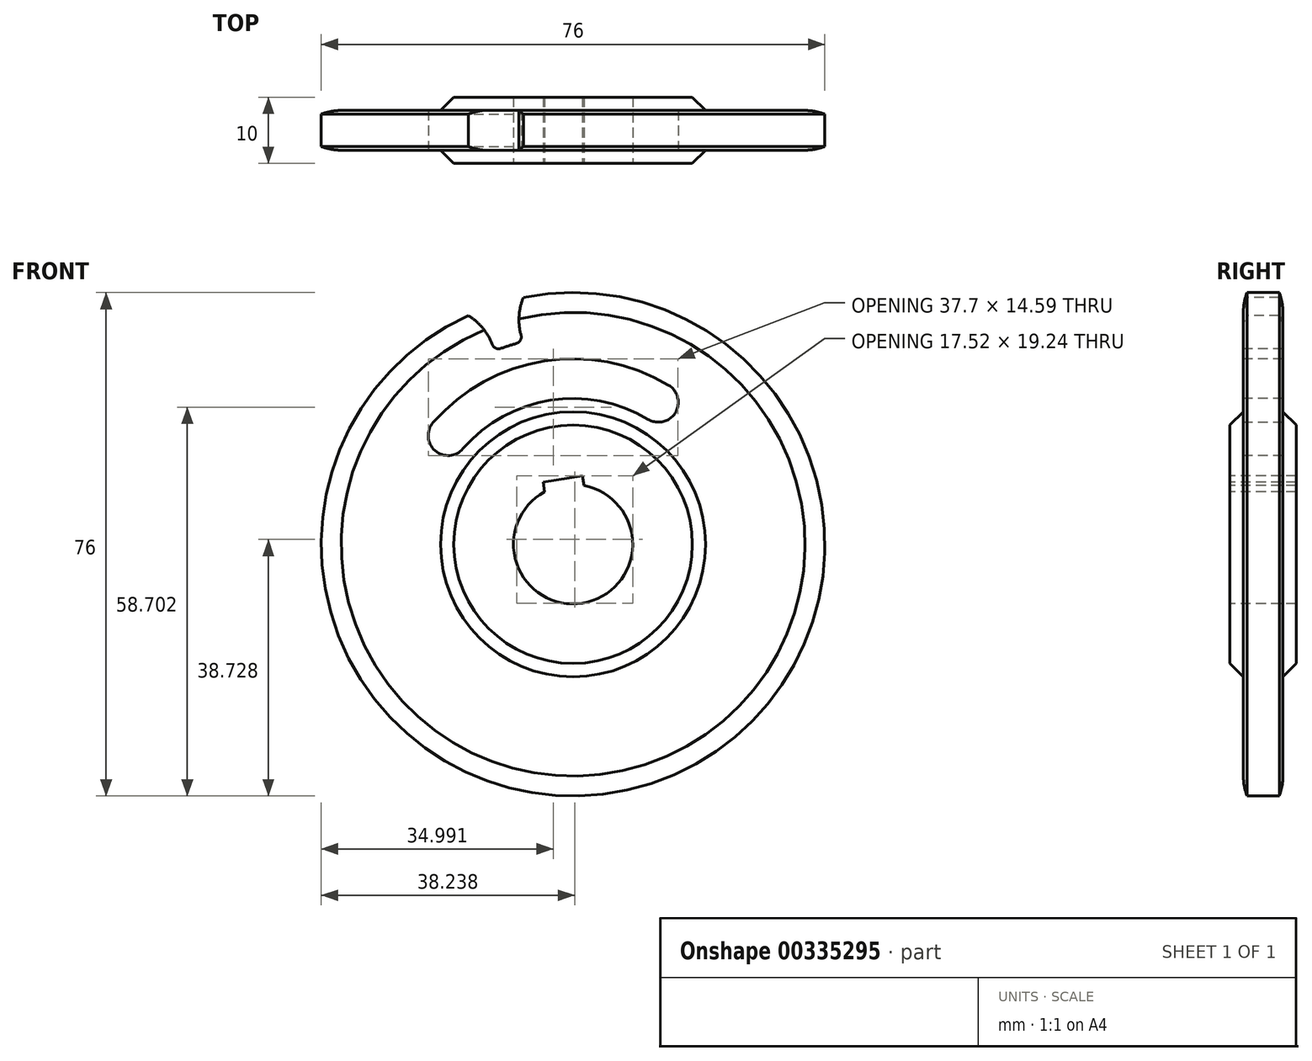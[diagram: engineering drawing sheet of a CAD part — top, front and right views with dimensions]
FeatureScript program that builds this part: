
annotation { "Feature Type Name" : "Feature", "Feature Type Description" : "" }
export const myFeature = defineFeature(function(context is Context, id is Id, definition is map)
    precondition{}
    {
        {
            var Q0;
            Q0=qCreatedBy(makeId("Front.planeOp"),FACE);
            var sketch = newSketch(context, id + "F0", { "sketchPlane" : qUnion([Q0])});
            skCircle(sketch, "E0", {"center": v(0, 0) * mm, "radius": 38 * mm});
            skSolve(sketch);
        }
        {
            var Q0;
            Q0=makeQuery(id+"F0.imprint","IMPRINT",FACE,{"disambiguationData":[TD([[makeQuery(id+"F0.imprint","IMPRINT",EDGE,{"derivedFrom":sQuery(id+"F0.wireOp",EDGE,"E0")}),1.0]])]});
            extrude(context, id + "F1", {"entities" : qUnion([Q0]), "depth" : 6 * mm, "symmetric" : true});
        }
        {
            var Q0;
            Q0=makeQuery(id+"F1.opExtrude","CAP_FACE",FACE,{"disambiguationData":[OSD([sQuery(id+"F0.wireOp",EDGE,"E0")])],"isStart":false});
            var sketch = newSketch(context, id + "F2", { "sketchPlane" : qUnion([Q0])});
            skLineSegment(sketch, "E1", {"start": v(0, 0) * mm, "end": v(0, 38) * mm, "construction": true});
            skArc(sketch, "E2", {"start": v(-1.57, 37.97) * mm, "mid": v(-0.79, 38) * mm, "end": v(0, 38) * mm, "construction": true});
            skCircle(sketch, "E3", {"center": v(0, 0) * mm, "radius": 35 * mm, "construction": true});
            skCircle(sketch, "E4", {"center": v(0, 0) * mm, "radius": 31.5 * mm, "construction": true});
            skArc(sketch, "E5", {"start": v(-1.58, 37.97) * mm, "mid": v(-2.67, 35.28) * mm, "end": v(-2.82, 32.39) * mm});
            skPoint(sketch, "E6", {"position": v(-2.75, 34.9) * mm});
            skLineSegment(sketch, "E7", {"start": v(0, 0) * mm, "end": v(-5.94, 37.53) * mm, "construction": true});
            skArc(sketch, "E8", {"start": v(-3.7, 31.28) * mm, "mid": v(-4.31, 31.2) * mm, "end": v(-4.93, 31.11) * mm});
            skPoint(sketch, "E9.visualSharp", {"position": v(-2.65, 31.39) * mm});
            skArc(sketch, "E9.filletArc", {"start": v(-3.7, 31.28) * mm, "mid": v(-3.03, 31.65) * mm, "end": v(-2.82, 32.39) * mm});
            skArc(sketch, "E10", {"start": v(-1.57, 37.97) * mm, "mid": v(-3.77, 37.81) * mm, "end": v(-5.94, 37.53) * mm});
            skArc(sketch, "E11.MirrorCS", {"start": v(-10.23, 36.6) * mm, "mid": v(-8.1, 37.13) * mm, "end": v(-5.94, 37.53) * mm});
            skArc(sketch, "E12.MirrorCS", {"start": v(-10.23, 36.6) * mm, "mid": v(-8.37, 34.38) * mm, "end": v(-7.32, 31.67) * mm});
            skArc(sketch, "E13.MirrorCS", {"start": v(-6.15, 30.9) * mm, "mid": v(-6.9, 31.04) * mm, "end": v(-7.32, 31.67) * mm});
            skArc(sketch, "E14.MirrorCS", {"start": v(-6.15, 30.9) * mm, "mid": v(-5.54, 31) * mm, "end": v(-4.93, 31.11) * mm});
            skSolve(sketch);
        }
        {
            var Q0;
            Q0=qSketchRegion(id+"F2",true);
            extrude(context, id + "F3", {"entities" : qUnion([Q0]), "operationType" : NewBodyOperationType.REMOVE, "oppositeDirection" : true, "depth" : 25 * mm});
        }
        {
            var Q0;
            Q0=qCreatedBy(makeId("Front.planeOp"),FACE);
            var sketch = newSketch(context, id + "F4", { "sketchPlane" : qUnion([Q0])});
            skCircle(sketch, "E15", {"center": v(0, 0) * mm, "radius": 18 * mm});
            skSolve(sketch);
        }
        {
            var Q0;
            Q0=qSketchRegion(id+"F4",true);
            extrude(context, id + "F5", {"entities" : qUnion([Q0]), "depth" : 10 * mm, "symmetric" : true});
        }
        {
            var Q0;
            Q0=makeQuery(id+"F1.opExtrude","SWEPT_BODY",BODY,{"disambiguationData":[OSD([sQuery(id+"F0.wireOp",EDGE,"E0")])]});
            var Q1;
            Q1=makeQuery(id+"F5.opExtrude","SWEPT_BODY",BODY,{"disambiguationData":[OSD([sQuery(id+"F4.wireOp",EDGE,"E15")])]});
            booleanBodies(context, id + "F6", {"operationType" : BooleanOperationType.UNION, "tools" : qUnion([Q0, Q1])});
        }
        {
            var Q0;
            Q0=makeQuery(id+"F6.opBoolean","INTERSECT",EDGE,{"derivedFrom":[makeQuery(id+"F1.opExtrude","CAP_FACE",FACE,{"disambiguationData":[OSD([sQuery(id+"F0.wireOp",EDGE,"E0")])],"isStart":true}),makeQuery(id+"F5.opExtrude","SWEPT_FACE",FACE,{"disambiguationData":[OSD([sQuery(id+"F4.wireOp",EDGE,"E15")])]})]});
            var Q1;
            Q1=makeQuery(id+"F6.opBoolean","INTERSECT",EDGE,{"derivedFrom":[makeQuery(id+"F1.opExtrude","CAP_FACE",FACE,{"disambiguationData":[OSD([sQuery(id+"F0.wireOp",EDGE,"E0")])],"isStart":false}),makeQuery(id+"F5.opExtrude","SWEPT_FACE",FACE,{"disambiguationData":[OSD([sQuery(id+"F4.wireOp",EDGE,"E15")])]})]});
            chamfer(context, id + "F7", {"entities" : qUnion([Q0, Q1]), "chamferType" : ChamferType.OFFSET_ANGLE, "width" : 2 * mm, "oppositeDirection" : false, "angle" : 45 * degree, "tangentPropagation" : true});
        }
        {
            var Q0;
            Q0=qCreatedBy(makeId("Right.planeOp"),FACE);
            var sketch = newSketch(context, id + "F8", { "sketchPlane" : qUnion([Q0])});
            skLineSegment(sketch, "E16", {"start": v(0, 0) * mm, "end": v(0, 51.39) * mm, "construction": true});
            skArc(sketch, "E17", {"start": v(-2.44, 38) * mm, "mid": v(-2.85, 36.52) * mm, "end": v(-3, 35) * mm});
            skArc(sketch, "E18", {"start": v(-2.44, 38) * mm, "mid": v(-4.7, 36.87) * mm, "end": v(-3, 35) * mm});
            skArc(sketch, "E19.MirrorCS", {"start": v(2.44, 38) * mm, "mid": v(4.7, 36.87) * mm, "end": v(3, 35) * mm});
            skArc(sketch, "E20.MirrorCS", {"start": v(2.44, 38) * mm, "mid": v(2.85, 36.52) * mm, "end": v(3, 35) * mm});
            skSolve(sketch);
        }
        {
            var Q0;
            Q0=qSketchRegion(id+"F8",true);
            var Q1;
            {var subQ0=sQuery(id+"F4.wireOp",EDGE,"E15");Q1=makeQuery(id+"F7.opChamfer","BLEND_EDGE",EDGE,{"blendedFrom":[makeQuery(id+"F6.opBoolean","INTERSECT",EDGE,{"derivedFrom":[makeQuery(id+"F1.opExtrude","CAP_FACE",FACE,{"disambiguationData":[OSD([sQuery(id+"F0.wireOp",EDGE,"E0")])],"isStart":false}),makeQuery(id+"F5.opExtrude","SWEPT_FACE",FACE,{"disambiguationData":[OSD([subQ0])]})]}),makeQuery(id+"F5.opExtrude","CAP_FACE",FACE,{"disambiguationData":[OSD([subQ0])],"isStart":false})],"blendedInto":[makeQuery(id+"F5.opExtrude","CAP_FACE",FACE,{"disambiguationData":[OSD([subQ0])],"isStart":false})]});}
            revolve(context, id + "F9", {"operationType" : NewBodyOperationType.REMOVE, "entities" : qUnion([Q0]), "axis" : qUnion([Q1]), "revolveType" : RevolveType.FULL, "oppositeDirection" : true});
        }
        {
            var Q0;
            Q0=makeQuery(id+"F5.opExtrude","CAP_FACE",FACE,{"disambiguationData":[OSD([sQuery(id+"F4.wireOp",EDGE,"E15")])],"isStart":false});
            var sketch = newSketch(context, id + "F10", { "sketchPlane" : qUnion([Q0])});
            skCircle(sketch, "E21", {"center": v(0, 0) * mm, "radius": 9 * mm});
            skSolve(sketch);
        }
        {
            var Q0;
            Q0=makeQuery(id+"F10.imprint","IMPRINT",FACE,{"disambiguationData":[TD([[makeQuery(id+"F10.imprint","IMPRINT",EDGE,{"derivedFrom":sQuery(id+"F10.wireOp",EDGE,"E21")}),1.0]])]});
            extrude(context, id + "F11", {"entities" : qUnion([Q0]), "operationType" : NewBodyOperationType.REMOVE, "oppositeDirection" : true, "depth" : 25 * mm});
        }
        {
            var Q0;
            Q0=makeQuery(id+"F5.opExtrude","CAP_FACE",FACE,{"disambiguationData":[OSD([sQuery(id+"F4.wireOp",EDGE,"E15")])],"isStart":false});
            var sketch = newSketch(context, id + "F12", { "sketchPlane" : qUnion([Q0])});
            skLineSegment(sketch, "E22.bottom", {"start": v(3, 10) * mm, "end": v(-3, 10) * mm});
            skLineSegment(sketch, "E22.top", {"start": v(3, 5.66) * mm, "end": v(-3, 5.66) * mm});
            skLineSegment(sketch, "E22.left", {"start": v(3, 10) * mm, "end": v(3, 5.66) * mm});
            skLineSegment(sketch, "E22.right", {"start": v(-3, 10) * mm, "end": v(-3, 5.66) * mm});
            skPoint(sketch, "E22.middle", {"position": v(0, 7.83) * mm});
            skSolve(sketch);
        }
        {
            var Q0;
            {var subQ0=sQuery(id+"F12.wireOp",EDGE,"E22.bottom");Q0=makeQuery(id+"F12.imprint","IMPRINT",FACE,{"disambiguationData":[TD([[makeQuery(id+"F12.imprint","IMPRINT",EDGE,{"derivedFrom":subQ0}),1.0]])]});}
            extrude(context, id + "F13", {"entities" : qUnion([Q0]), "operationType" : NewBodyOperationType.REMOVE, "oppositeDirection" : true, "depth" : 25 * mm});
        }
        {
            var Q0;
            Q0=makeQuery(id+"F1.opExtrude","CAP_FACE",FACE,{"disambiguationData":[OSD([sQuery(id+"F0.wireOp",EDGE,"E0")])],"isStart":false});
            var sketch = newSketch(context, id + "F14", { "sketchPlane" : qUnion([Q0])});
            skLineSegment(sketch, "E23", {"start": v(0, 0) * mm, "end": v(-16.07, 19.15) * mm, "construction": true});
            skLineSegment(sketch, "E24", {"start": v(0, 0) * mm, "end": v(0, 26.53) * mm, "construction": true});
            skLineSegment(sketch, "E25", {"start": v(0, 0) * mm, "end": v(16.07, 19.15) * mm, "construction": true});
            skCircle(sketch, "E26", {"center": v(0, 0) * mm, "radius": 25 * mm, "construction": true});
            skArc(sketch, "E27", {"start": v(-18, 21.45) * mm, "mid": v(-18.37, 17.22) * mm, "end": v(-14.14, 16.85) * mm});
            skArc(sketch, "E28", {"start": v(13.66, 20.94) * mm, "mid": v(16.42, 16.17) * mm, "end": v(18, 21.45) * mm});
            skArc(sketch, "E29", {"start": v(-18, 21.45) * mm, "mid": v(0, 28) * mm, "end": v(18, 21.45) * mm});
            skArc(sketch, "E30", {"start": v(-14.14, 16.85) * mm, "mid": v(0, 22) * mm, "end": v(14.14, 16.85) * mm});
            skSolve(sketch);
        }
        {
            var Q0;
            Q0=qSketchRegion(id+"F14",true);
            extrude(context, id + "F15", {"entities" : qUnion([Q0]), "operationType" : NewBodyOperationType.REMOVE, "oppositeDirection" : true, "depth" : 25 * mm});
        }
        {
            var Q0;
            Q0=makeQuery(id+"F1.opExtrude","SWEPT_BODY",BODY,{"disambiguationData":[OSD([sQuery(id+"F0.wireOp",EDGE,"E0")])]});
            var Q1;
            {var subQ0=sQuery(id+"F4.wireOp",EDGE,"E15");Q1=makeQuery(id+"F7.opChamfer","BLEND_EDGE",EDGE,{"blendedFrom":[makeQuery(id+"F6.opBoolean","INTERSECT",EDGE,{"derivedFrom":[makeQuery(id+"F1.opExtrude","CAP_FACE",FACE,{"disambiguationData":[OSD([sQuery(id+"F0.wireOp",EDGE,"E0")])],"isStart":false}),makeQuery(id+"F5.opExtrude","SWEPT_FACE",FACE,{"disambiguationData":[OSD([subQ0])]})]}),makeQuery(id+"F5.opExtrude","CAP_FACE",FACE,{"disambiguationData":[OSD([subQ0])],"isStart":false})],"blendedInto":[makeQuery(id+"F5.opExtrude","CAP_FACE",FACE,{"disambiguationData":[OSD([subQ0])],"isStart":false})]});}
            transform(context, id + "F16", {"entities" : qUnion([Q0]), "transformType" : TransformType.ROTATION, "transformAxis" : qUnion([Q1]), "angle" : 9 * degree, "makeCopy" : false});
        }
    });
